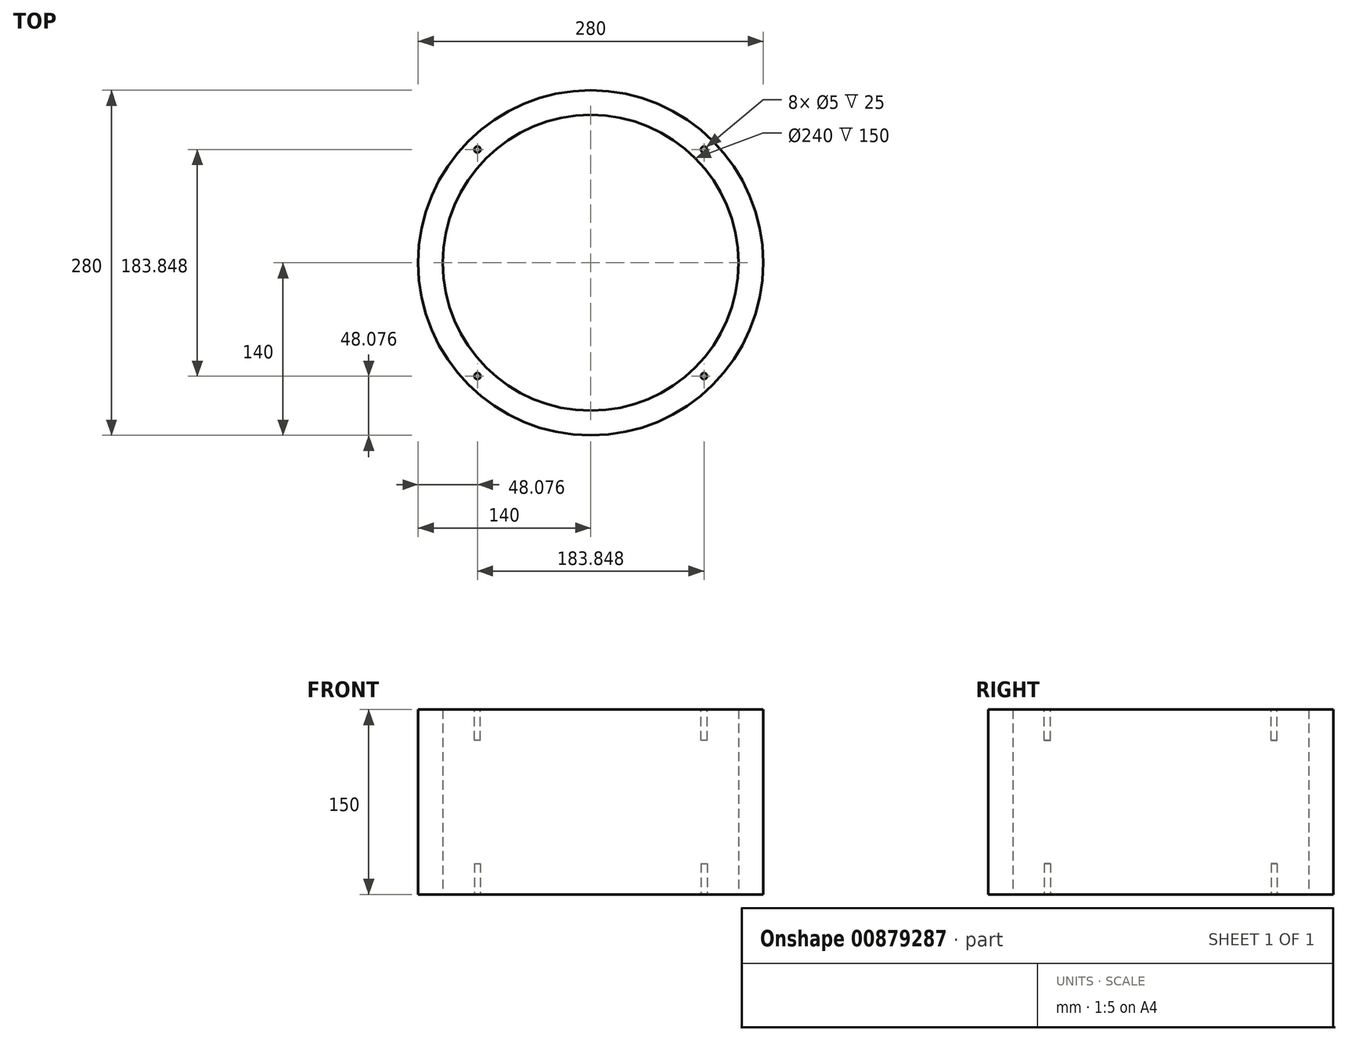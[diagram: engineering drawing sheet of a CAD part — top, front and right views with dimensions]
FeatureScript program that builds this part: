
annotation { "Feature Type Name" : "Feature", "Feature Type Description" : "" }
export const myFeature = defineFeature(function(context is Context, id is Id, definition is map)
    precondition{}
    {
        {
            var Q0;
            Q0=qCreatedBy(makeId("Top.planeOp"),FACE);
            var sketch = newSketch(context, id + "F0", { "sketchPlane" : qUnion([Q0])});
            skCircle(sketch, "E0", {"center": v(0, 0) * mm, "radius": 140 * mm});
            skCircle(sketch, "E1", {"center": v(0, 0) * mm, "radius": 120 * mm});
            skSolve(sketch);
        }
        {
            var Q0;
            Q0=makeQuery(id+"F0.imprint","IMPRINT",FACE,{"disambiguationData":[TD([[makeQuery(id+"F0.imprint","IMPRINT",EDGE,{"derivedFrom":sQuery(id+"F0.wireOp",EDGE,"E0")}),1.0]])]});
            extrude(context, id + "F1", {"entities" : qUnion([Q0]), "depth" : 150 * mm, "offsetDistance" : 25 * mm});
        }
        {
            var Q0;
            Q0=makeQuery(id+"F1.opExtrude","CAP_FACE",FACE,{"disambiguationData":[OSD([sQuery(id+"F0.wireOp",EDGE,"E0"),sQuery(id+"F0.wireOp",EDGE,"E1")])],"isStart":false});
            var sketch = newSketch(context, id + "F2", { "sketchPlane" : qUnion([Q0])});
            skCircle(sketch, "E2", {"center": v(0, 0) * mm, "radius": 130 * mm});
            skLineSegment(sketch, "E3", {"start": v(-91.92, 91.92) * mm, "end": v(0, 0) * mm});
            skLineSegment(sketch, "E4", {"start": v(0, 0) * mm, "end": v(91.92, -91.92) * mm});
            skLineSegment(sketch, "E5", {"start": v(0, 0) * mm, "end": v(91.92, 91.92) * mm});
            skLineSegment(sketch, "E6", {"start": v(0, 0) * mm, "end": v(-91.92, -91.92) * mm});
            skCircle(sketch, "E7", {"center": v(-91.92, 91.92) * mm, "radius": 2.5 * mm});
            skCircle(sketch, "E8", {"center": v(91.92, 91.92) * mm, "radius": 2.5 * mm});
            skCircle(sketch, "E9", {"center": v(91.92, -91.92) * mm, "radius": 2.5 * mm});
            skCircle(sketch, "E10", {"center": v(-91.92, -91.92) * mm, "radius": 2.5 * mm});
            skSolve(sketch);
        }
        {
            var Q0;
            {var subQ0=sQuery(id+"F2.wireOp",EDGE,"E2");var subQ1=makeQuery(id+"F2.imprint","INTERSECT",VERTEX,{"derivedFrom":[subQ0,sQuery(id+"F2.wireOp",EDGE,"E3")]});Q0=makeQuery(id+"F2.imprint","IMPRINT",FACE,{"disambiguationData":[TD([[makeQuery(id+"F2.imprint","IMPRINT",EDGE,{"disambiguationData":[TD([[subQ1,1.0]])],"derivedFrom":subQ0}),-1.0]])]});}
            var Q1;
            {var subQ0=sQuery(id+"F2.wireOp",EDGE,"E3");var subQ1=sQuery(id+"F2.wireOp",EDGE,"E2");var subQ2=makeQuery(id+"F2.imprint","INTERSECT",VERTEX,{"derivedFrom":[subQ1,subQ0]});Q1=makeQuery(id+"F2.imprint","IMPRINT",FACE,{"disambiguationData":[TD([[makeQuery(id+"F2.imprint","IMPRINT",EDGE,{"disambiguationData":[TD([[subQ2,1.0]])],"derivedFrom":subQ1}),1.0]])]});}
            var Q2;
            {var subQ0=sQuery(id+"F2.wireOp",EDGE,"E3");var subQ1=sQuery(id+"F2.wireOp",EDGE,"E2");var subQ2=makeQuery(id+"F2.imprint","INTERSECT",VERTEX,{"derivedFrom":[subQ1,subQ0]});Q2=makeQuery(id+"F2.imprint","IMPRINT",FACE,{"disambiguationData":[TD([[makeQuery(id+"F2.imprint","IMPRINT",EDGE,{"disambiguationData":[TD([[subQ2,-1.0]])],"derivedFrom":subQ1}),1.0]])]});}
            var Q3;
            {var subQ0=sQuery(id+"F2.wireOp",EDGE,"E2");var subQ1=makeQuery(id+"F2.imprint","INTERSECT",VERTEX,{"derivedFrom":[subQ0,sQuery(id+"F2.wireOp",EDGE,"E5")]});Q3=makeQuery(id+"F2.imprint","IMPRINT",FACE,{"disambiguationData":[TD([[makeQuery(id+"F2.imprint","IMPRINT",EDGE,{"disambiguationData":[TD([[subQ1,1.0]])],"derivedFrom":subQ0}),-1.0]])]});}
            var Q4;
            {var subQ0=sQuery(id+"F2.wireOp",EDGE,"E5");var subQ1=sQuery(id+"F2.wireOp",EDGE,"E2");var subQ2=makeQuery(id+"F2.imprint","INTERSECT",VERTEX,{"derivedFrom":[subQ1,subQ0]});Q4=makeQuery(id+"F2.imprint","IMPRINT",FACE,{"disambiguationData":[TD([[makeQuery(id+"F2.imprint","IMPRINT",EDGE,{"disambiguationData":[TD([[subQ2,1.0]])],"derivedFrom":subQ1}),1.0]])]});}
            var Q5;
            {var subQ0=sQuery(id+"F2.wireOp",EDGE,"E5");var subQ1=sQuery(id+"F2.wireOp",EDGE,"E2");var subQ2=makeQuery(id+"F2.imprint","INTERSECT",VERTEX,{"derivedFrom":[subQ1,subQ0]});Q5=makeQuery(id+"F2.imprint","IMPRINT",FACE,{"disambiguationData":[TD([[makeQuery(id+"F2.imprint","IMPRINT",EDGE,{"disambiguationData":[TD([[subQ2,-1.0]])],"derivedFrom":subQ1}),1.0]])]});}
            var Q6;
            {var subQ0=sQuery(id+"F2.wireOp",EDGE,"E4");var subQ1=sQuery(id+"F2.wireOp",EDGE,"E2");var subQ2=makeQuery(id+"F2.imprint","INTERSECT",VERTEX,{"derivedFrom":[subQ1,subQ0]});Q6=makeQuery(id+"F2.imprint","IMPRINT",FACE,{"disambiguationData":[TD([[makeQuery(id+"F2.imprint","IMPRINT",EDGE,{"disambiguationData":[TD([[subQ2,-1.0]])],"derivedFrom":subQ1}),1.0]])]});}
            var Q7;
            {var subQ0=sQuery(id+"F2.wireOp",EDGE,"E4");var subQ1=sQuery(id+"F2.wireOp",EDGE,"E2");var subQ2=makeQuery(id+"F2.imprint","INTERSECT",VERTEX,{"derivedFrom":[subQ1,subQ0]});Q7=makeQuery(id+"F2.imprint","IMPRINT",FACE,{"disambiguationData":[TD([[makeQuery(id+"F2.imprint","IMPRINT",EDGE,{"disambiguationData":[TD([[subQ2,1.0]])],"derivedFrom":subQ1}),1.0]])]});}
            var Q8;
            {var subQ0=sQuery(id+"F2.wireOp",EDGE,"E2");var subQ1=makeQuery(id+"F2.imprint","INTERSECT",VERTEX,{"derivedFrom":[subQ0,sQuery(id+"F2.wireOp",EDGE,"E4")]});Q8=makeQuery(id+"F2.imprint","IMPRINT",FACE,{"disambiguationData":[TD([[makeQuery(id+"F2.imprint","IMPRINT",EDGE,{"disambiguationData":[TD([[subQ1,1.0]])],"derivedFrom":subQ0}),-1.0]])]});}
            var Q9;
            {var subQ0=sQuery(id+"F2.wireOp",EDGE,"E6");var subQ1=sQuery(id+"F2.wireOp",EDGE,"E2");var subQ2=makeQuery(id+"F2.imprint","INTERSECT",VERTEX,{"derivedFrom":[subQ1,subQ0]});Q9=makeQuery(id+"F2.imprint","IMPRINT",FACE,{"disambiguationData":[TD([[makeQuery(id+"F2.imprint","IMPRINT",EDGE,{"disambiguationData":[TD([[subQ2,1.0]])],"derivedFrom":subQ1}),1.0]])]});}
            var Q10;
            {var subQ0=sQuery(id+"F2.wireOp",EDGE,"E6");var subQ1=sQuery(id+"F2.wireOp",EDGE,"E2");var subQ2=makeQuery(id+"F2.imprint","INTERSECT",VERTEX,{"derivedFrom":[subQ1,subQ0]});Q10=makeQuery(id+"F2.imprint","IMPRINT",FACE,{"disambiguationData":[TD([[makeQuery(id+"F2.imprint","IMPRINT",EDGE,{"disambiguationData":[TD([[subQ2,-1.0]])],"derivedFrom":subQ1}),1.0]])]});}
            var Q11;
            {var subQ0=sQuery(id+"F2.wireOp",EDGE,"E2");var subQ1=makeQuery(id+"F2.imprint","INTERSECT",VERTEX,{"derivedFrom":[subQ0,sQuery(id+"F2.wireOp",EDGE,"E6")]});Q11=makeQuery(id+"F2.imprint","IMPRINT",FACE,{"disambiguationData":[TD([[makeQuery(id+"F2.imprint","IMPRINT",EDGE,{"disambiguationData":[TD([[subQ1,1.0]])],"derivedFrom":subQ0}),-1.0]])]});}
            extrude(context, id + "F3", {"entities" : qUnion([Q0, Q1, Q2, Q3, Q4, Q5, Q6, Q7, Q8, Q9, Q10, Q11]), "operationType" : NewBodyOperationType.REMOVE, "oppositeDirection" : true, "depth" : 25 * mm, "offsetDistance" : 25 * mm});
        }
        {
            var Q0;
            Q0=makeQuery(id+"F1.opExtrude","CAP_FACE",FACE,{"disambiguationData":[OSD([sQuery(id+"F0.wireOp",EDGE,"E0"),sQuery(id+"F0.wireOp",EDGE,"E1")])],"isStart":true});
            var sketch = newSketch(context, id + "F4", { "sketchPlane" : qUnion([Q0])});
            skCircle(sketch, "E11", {"center": v(0, 0) * mm, "radius": 130 * mm});
            skLineSegment(sketch, "E12", {"start": v(0, 0) * mm, "end": v(-91.92, 91.92) * mm});
            skLineSegment(sketch, "E13", {"start": v(0, 0) * mm, "end": v(91.92, -91.92) * mm});
            skLineSegment(sketch, "E14", {"start": v(0, 0) * mm, "end": v(-91.92, -91.92) * mm});
            skLineSegment(sketch, "E15", {"start": v(0, 0) * mm, "end": v(91.92, 91.92) * mm});
            skCircle(sketch, "E16", {"center": v(-91.92, 91.92) * mm, "radius": 2.5 * mm});
            skCircle(sketch, "E17", {"center": v(91.92, 91.92) * mm, "radius": 2.5 * mm});
            skCircle(sketch, "E18", {"center": v(91.92, -91.92) * mm, "radius": 2.5 * mm});
            skCircle(sketch, "E19", {"center": v(-91.92, -91.92) * mm, "radius": 2.5 * mm});
            skSolve(sketch);
        }
        {
            var Q0;
            {var subQ0=sQuery(id+"F4.wireOp",EDGE,"E11");var subQ1=makeQuery(id+"F4.imprint","INTERSECT",VERTEX,{"derivedFrom":[subQ0,sQuery(id+"F4.wireOp",EDGE,"E12")]});Q0=makeQuery(id+"F4.imprint","IMPRINT",FACE,{"disambiguationData":[TD([[makeQuery(id+"F4.imprint","IMPRINT",EDGE,{"disambiguationData":[TD([[subQ1,1.0]])],"derivedFrom":subQ0}),-1.0]])]});}
            var Q1;
            {var subQ0=sQuery(id+"F4.wireOp",EDGE,"E12");var subQ1=sQuery(id+"F4.wireOp",EDGE,"E11");var subQ2=makeQuery(id+"F4.imprint","INTERSECT",VERTEX,{"derivedFrom":[subQ1,subQ0]});Q1=makeQuery(id+"F4.imprint","IMPRINT",FACE,{"disambiguationData":[TD([[makeQuery(id+"F4.imprint","IMPRINT",EDGE,{"disambiguationData":[TD([[subQ2,1.0]])],"derivedFrom":subQ1}),1.0]])]});}
            var Q2;
            {var subQ0=sQuery(id+"F4.wireOp",EDGE,"E12");var subQ1=sQuery(id+"F4.wireOp",EDGE,"E11");var subQ2=makeQuery(id+"F4.imprint","INTERSECT",VERTEX,{"derivedFrom":[subQ1,subQ0]});Q2=makeQuery(id+"F4.imprint","IMPRINT",FACE,{"disambiguationData":[TD([[makeQuery(id+"F4.imprint","IMPRINT",EDGE,{"disambiguationData":[TD([[subQ2,-1.0]])],"derivedFrom":subQ1}),1.0]])]});}
            var Q3;
            {var subQ0=sQuery(id+"F4.wireOp",EDGE,"E14");var subQ1=sQuery(id+"F4.wireOp",EDGE,"E11");var subQ2=makeQuery(id+"F4.imprint","INTERSECT",VERTEX,{"derivedFrom":[subQ1,subQ0]});Q3=makeQuery(id+"F4.imprint","IMPRINT",FACE,{"disambiguationData":[TD([[makeQuery(id+"F4.imprint","IMPRINT",EDGE,{"disambiguationData":[TD([[subQ2,-1.0]])],"derivedFrom":subQ1}),1.0]])]});}
            var Q4;
            {var subQ0=sQuery(id+"F4.wireOp",EDGE,"E14");var subQ1=sQuery(id+"F4.wireOp",EDGE,"E11");var subQ2=makeQuery(id+"F4.imprint","INTERSECT",VERTEX,{"derivedFrom":[subQ1,subQ0]});Q4=makeQuery(id+"F4.imprint","IMPRINT",FACE,{"disambiguationData":[TD([[makeQuery(id+"F4.imprint","IMPRINT",EDGE,{"disambiguationData":[TD([[subQ2,1.0]])],"derivedFrom":subQ1}),1.0]])]});}
            var Q5;
            {var subQ0=sQuery(id+"F4.wireOp",EDGE,"E11");var subQ1=makeQuery(id+"F4.imprint","INTERSECT",VERTEX,{"derivedFrom":[subQ0,sQuery(id+"F4.wireOp",EDGE,"E14")]});Q5=makeQuery(id+"F4.imprint","IMPRINT",FACE,{"disambiguationData":[TD([[makeQuery(id+"F4.imprint","IMPRINT",EDGE,{"disambiguationData":[TD([[subQ1,1.0]])],"derivedFrom":subQ0}),-1.0]])]});}
            var Q6;
            {var subQ0=sQuery(id+"F4.wireOp",EDGE,"E11");var subQ1=makeQuery(id+"F4.imprint","INTERSECT",VERTEX,{"derivedFrom":[subQ0,sQuery(id+"F4.wireOp",EDGE,"E13")]});Q6=makeQuery(id+"F4.imprint","IMPRINT",FACE,{"disambiguationData":[TD([[makeQuery(id+"F4.imprint","IMPRINT",EDGE,{"disambiguationData":[TD([[subQ1,1.0]])],"derivedFrom":subQ0}),-1.0]])]});}
            var Q7;
            {var subQ0=sQuery(id+"F4.wireOp",EDGE,"E13");var subQ1=sQuery(id+"F4.wireOp",EDGE,"E11");var subQ2=makeQuery(id+"F4.imprint","INTERSECT",VERTEX,{"derivedFrom":[subQ1,subQ0]});Q7=makeQuery(id+"F4.imprint","IMPRINT",FACE,{"disambiguationData":[TD([[makeQuery(id+"F4.imprint","IMPRINT",EDGE,{"disambiguationData":[TD([[subQ2,1.0]])],"derivedFrom":subQ1}),1.0]])]});}
            var Q8;
            {var subQ0=sQuery(id+"F4.wireOp",EDGE,"E13");var subQ1=sQuery(id+"F4.wireOp",EDGE,"E11");var subQ2=makeQuery(id+"F4.imprint","INTERSECT",VERTEX,{"derivedFrom":[subQ1,subQ0]});Q8=makeQuery(id+"F4.imprint","IMPRINT",FACE,{"disambiguationData":[TD([[makeQuery(id+"F4.imprint","IMPRINT",EDGE,{"disambiguationData":[TD([[subQ2,-1.0]])],"derivedFrom":subQ1}),1.0]])]});}
            var Q9;
            {var subQ0=sQuery(id+"F4.wireOp",EDGE,"E15");var subQ1=sQuery(id+"F4.wireOp",EDGE,"E11");var subQ2=makeQuery(id+"F4.imprint","INTERSECT",VERTEX,{"derivedFrom":[subQ1,subQ0]});Q9=makeQuery(id+"F4.imprint","IMPRINT",FACE,{"disambiguationData":[TD([[makeQuery(id+"F4.imprint","IMPRINT",EDGE,{"disambiguationData":[TD([[subQ2,1.0]])],"derivedFrom":subQ1}),1.0]])]});}
            var Q10;
            {var subQ0=sQuery(id+"F4.wireOp",EDGE,"E15");var subQ1=sQuery(id+"F4.wireOp",EDGE,"E11");var subQ2=makeQuery(id+"F4.imprint","INTERSECT",VERTEX,{"derivedFrom":[subQ1,subQ0]});Q10=makeQuery(id+"F4.imprint","IMPRINT",FACE,{"disambiguationData":[TD([[makeQuery(id+"F4.imprint","IMPRINT",EDGE,{"disambiguationData":[TD([[subQ2,-1.0]])],"derivedFrom":subQ1}),1.0]])]});}
            var Q11;
            {var subQ0=sQuery(id+"F4.wireOp",EDGE,"E11");var subQ1=makeQuery(id+"F4.imprint","INTERSECT",VERTEX,{"derivedFrom":[subQ0,sQuery(id+"F4.wireOp",EDGE,"E15")]});Q11=makeQuery(id+"F4.imprint","IMPRINT",FACE,{"disambiguationData":[TD([[makeQuery(id+"F4.imprint","IMPRINT",EDGE,{"disambiguationData":[TD([[subQ1,1.0]])],"derivedFrom":subQ0}),-1.0]])]});}
            extrude(context, id + "F5", {"entities" : qUnion([Q0, Q1, Q2, Q3, Q4, Q5, Q6, Q7, Q8, Q9, Q10, Q11]), "operationType" : NewBodyOperationType.REMOVE, "oppositeDirection" : true, "depth" : 25 * mm, "offsetDistance" : 25 * mm});
        }
    });
